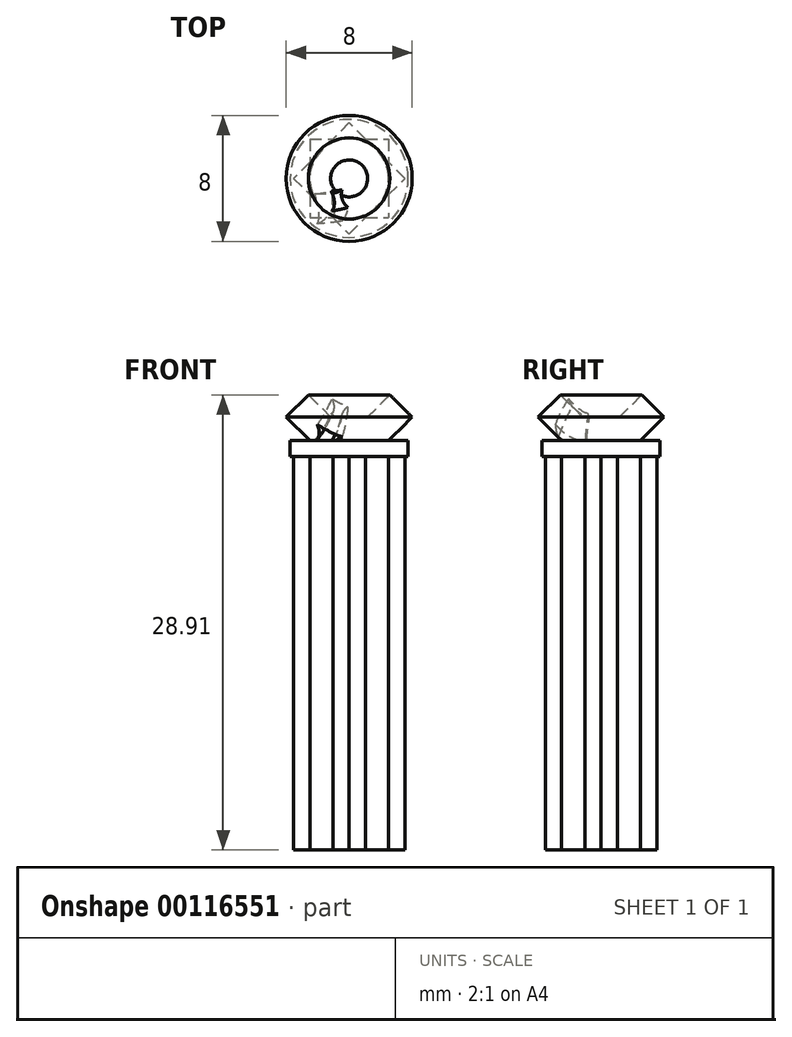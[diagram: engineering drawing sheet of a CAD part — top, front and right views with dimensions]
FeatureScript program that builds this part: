
annotation { "Feature Type Name" : "Feature", "Feature Type Description" : "" }
export const myFeature = defineFeature(function(context is Context, id is Id, definition is map)
    precondition{}
    {
        {
            var Q0;
            Q0=qCreatedBy(makeId("Front.planeOp"),FACE);
            var sketch = newSketch(context, id + "F0", { "sketchPlane" : qUnion([Q0])});
            skLineSegment(sketch, "E0", {"start": v(0, 0) * mm, "end": v(-1.17, 0) * mm});
            skLineSegment(sketch, "E1", {"start": v(-1.17, 0) * mm, "end": v(-2.59, 1.41) * mm});
            skLineSegment(sketch, "E2", {"start": v(-2.59, 1.41) * mm, "end": v(-4, 0) * mm});
            skLineSegment(sketch, "E3", {"start": v(-4, 0) * mm, "end": v(-2.5, -1.5) * mm});
            skLineSegment(sketch, "E4", {"start": v(-2.5, -1.5) * mm, "end": v(0, -1.5) * mm});
            skLineSegment(sketch, "E5", {"start": v(0, 0) * mm, "end": v(0, -1.5) * mm});
            skSolve(sketch);
        }
        {
            var Q0;
            Q0=makeQuery(id+"F0.imprint","IMPRINT",FACE,{"disambiguationData":[TD([[makeQuery(id+"F0.imprint","IMPRINT",EDGE,{"derivedFrom":sQuery(id+"F0.wireOp",EDGE,"E0")}),1.0]])]});
            var Q1;
            Q1=sQuery(id+"F0.wireOp",EDGE,"E5");
            revolve(context, id + "F1", {"entities" : qUnion([Q0]), "axis" : qUnion([Q1]), "revolveType" : RevolveType.FULL});
        }
        {
            var Q0;
            Q0=qCreatedBy(makeId("Front.planeOp"),FACE);
            var sketch = newSketch(context, id + "F2", { "sketchPlane" : qUnion([Q0])});
            skLineSegment(sketch, "E6", {"start": v(0, 0) * mm, "end": v(0, 4) * mm, "construction": true});
            skLineSegment(sketch, "E7", {"start": v(0, 4) * mm, "end": v(-4, 0) * mm, "construction": true});
            skLineSegment(sketch, "E8", {"start": v(-4, 0) * mm, "end": v(-2.48, -1.52) * mm, "construction": true});
            skSolve(sketch);
        }
        {
            var Q0;
            Q0=sQuery(id+"F2.wireOp",EDGE,"E8");
            cPlane(context, id + "F3", {"entities" : qUnion([Q0]), "cplaneType" : CPlaneType.LINE_ANGLE, "offset" : 25 * mm, "angle" : 90 * degree, "width" : 150 * mm, "height" : 150 * mm});
        }
        {
            var Q0;
            Q0=qCreatedBy(id+"F3.planeOp",FACE);
            var sketch = newSketch(context, id + "F4", { "sketchPlane" : qUnion([Q0])});
            skLineSegment(sketch, "E9", {"start": v(-0.98, 0) * mm, "end": v(-0.98, 0.5) * mm});
            skArc(sketch, "E10", {"start": v(-3.03, 1) * mm, "mid": v(-2.07, 0.48) * mm, "end": v(-0.98, 0.5) * mm});
            skLineSegment(sketch, "E11", {"start": v(-3.03, 1) * mm, "end": v(-3.03, 0) * mm});
            skLineSegment(sketch, "E12", {"start": v(-3.03, 0) * mm, "end": v(-0.98, 0) * mm});
            skLineSegment(sketch, "E13.MirrorCS", {"start": v(-3.03, -1) * mm, "end": v(-3.03, 0) * mm});
            skArc(sketch, "E14.MirrorCS", {"start": v(-3.03, -1) * mm, "mid": v(-2.07, -0.48) * mm, "end": v(-0.98, -0.5) * mm});
            skLineSegment(sketch, "E15.MirrorCS", {"start": v(-0.98, 0) * mm, "end": v(-0.98, -0.5) * mm});
            skSolve(sketch);
        }
        {
            var Q0;
            Q0 = qSketchRegion(id + "F4", true);
            var Q1;
            Q1=sQuery(id+"F2.wireOp",VERTEX,"E7.start");
            loft(context, id + "F5", {"operationType" : NewBodyOperationType.REMOVE, "startCondition" : LoftEndDerivativeType.NORMAL_TO_PROFILE, "startMagnitude" : 1, "sheetProfilesArray" : [{ "sheetProfileEntities" : qUnion([Q0]) }, { "sheetProfileEntities" : qUnion([Q1]) }]});
        }
        {
            var Q0;
            Q0=makeQuery(id+"F1.opRevolve","SWEPT_FACE",FACE,{"disambiguationData":[OSD([sQuery(id+"F0.wireOp",EDGE,"E4")])]});
            var sketch = newSketch(context, id + "F6", { "sketchPlane" : qUnion([Q0])});
            skCircle(sketch, "E16", {"center": v(0, 0) * mm, "radius": 3.75 * mm});
            skSolve(sketch);
        }
        {
            var Q0;
            Q0 = qSketchRegion(id + "F6", true);
            extrude(context, id + "F7", {"entities" : qUnion([Q0]), "operationType" : NewBodyOperationType.ADD, "depth" : 1 * mm});
        }
        {
            var Q0;
            Q0=makeQuery(id+"F7.opExtrude","CAP_FACE",FACE,{"disambiguationData":[OSD([sQuery(id+"F6.wireOp",EDGE,"E16")])],"isStart":false});
            var sketch = newSketch(context, id + "F8", { "sketchPlane" : qUnion([Q0])});
            skLineSegment(sketch, "E17.bottom", {"start": v(-2.5, -2.5) * mm, "end": v(2.5, -2.5) * mm});
            skLineSegment(sketch, "E17.top", {"start": v(-2.5, 2.5) * mm, "end": v(2.5, 2.5) * mm});
            skLineSegment(sketch, "E17.left", {"start": v(-2.5, -2.5) * mm, "end": v(-2.5, 2.5) * mm});
            skLineSegment(sketch, "E17.right", {"start": v(2.5, -2.5) * mm, "end": v(2.5, 2.5) * mm});
            skPoint(sketch, "E17.middle", {"position": v(0, 0) * mm});
            skLineSegment(sketch, "E18", {"start": v(0, 3.54) * mm, "end": v(3.54, 0) * mm});
            skLineSegment(sketch, "E19", {"start": v(3.54, 0) * mm, "end": v(0, -3.54) * mm});
            skLineSegment(sketch, "E20", {"start": v(0, -3.54) * mm, "end": v(-3.54, 0) * mm});
            skLineSegment(sketch, "E21", {"start": v(-3.54, 0) * mm, "end": v(0, 3.54) * mm});
            skSolve(sketch);
        }
        {
            var Q0;
            Q0 = qSketchRegion(id + "F8", true);
            extrude(context, id + "F9", {"entities" : qUnion([Q0]), "operationType" : NewBodyOperationType.ADD, "depth" : 25 * mm});
        }
    });
